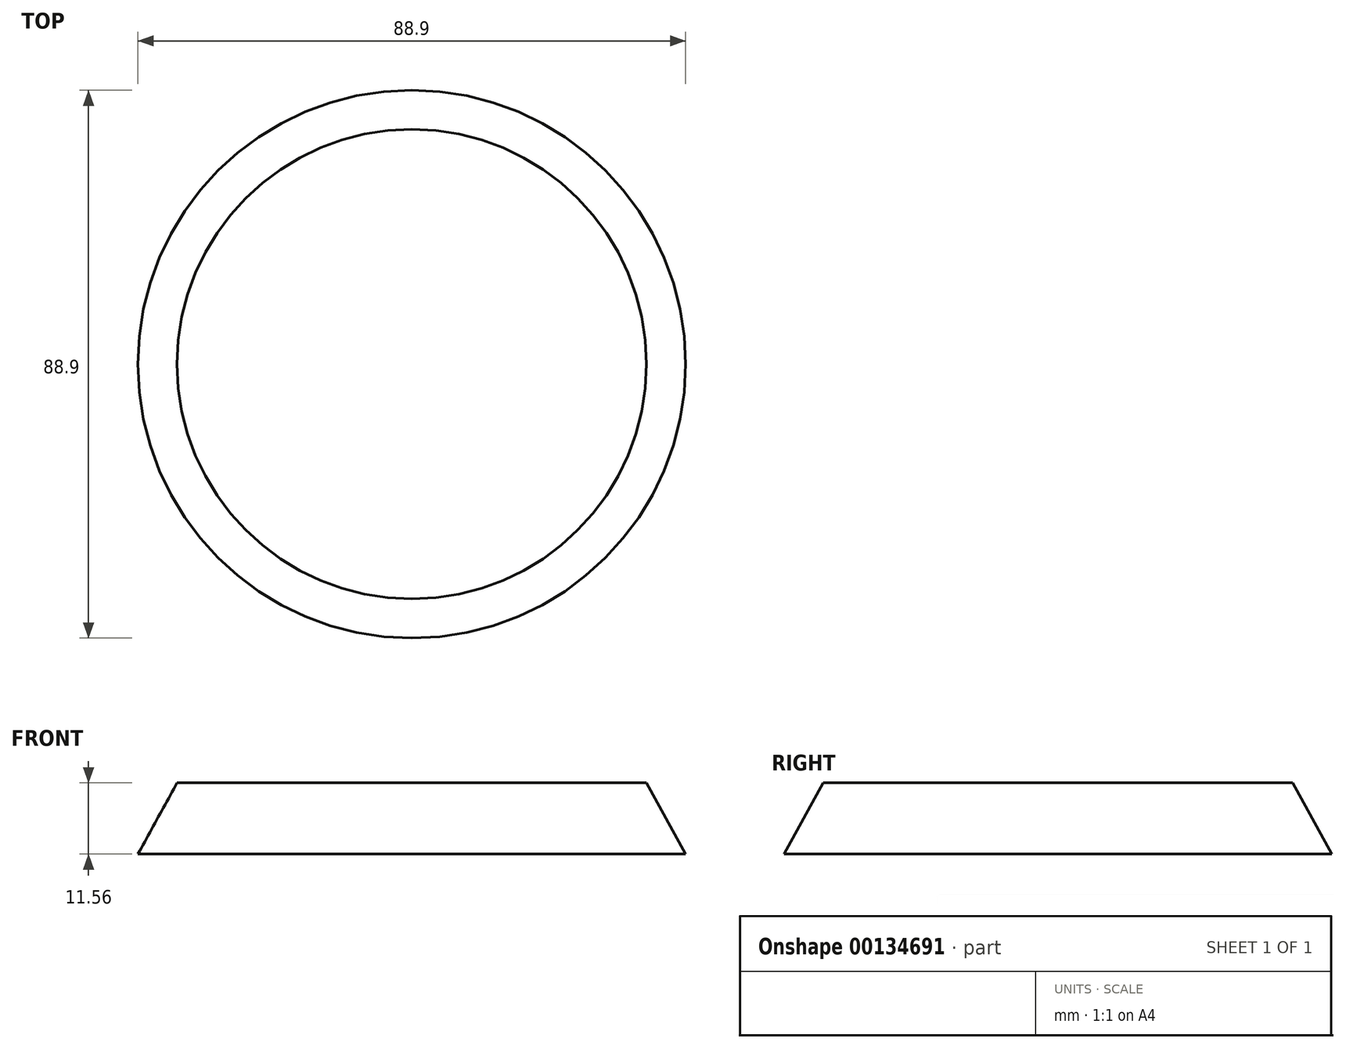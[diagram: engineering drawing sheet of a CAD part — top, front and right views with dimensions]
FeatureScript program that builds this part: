
annotation { "Feature Type Name" : "Feature", "Feature Type Description" : "" }
export const myFeature = defineFeature(function(context is Context, id is Id, definition is map)
    precondition{}
    {
        {
            var Q0;
            Q0=qCreatedBy(makeId("Front.planeOp"),FACE);
            var sketch = newSketch(context, id + "F0", { "sketchPlane" : qUnion([Q0])});
            skLineSegment(sketch, "E0", {"start": v(0, 11.56) * mm, "end": v(38.1, 11.56) * mm});
            skLineSegment(sketch, "E1", {"start": v(38.1, 11.56) * mm, "end": v(44.45, 0) * mm});
            skLineSegment(sketch, "E2", {"start": v(44.45, 0) * mm, "end": v(0, 0) * mm});
            skLineSegment(sketch, "E3", {"start": v(0, 0) * mm, "end": v(0, 11.56) * mm});
            skSolve(sketch);
        }
        {
            var Q0;
            Q0=makeQuery(id+"F0.imprint","IMPRINT",FACE,{"disambiguationData":[TD([[makeQuery(id+"F0.imprint","IMPRINT",EDGE,{"derivedFrom":sQuery(id+"F0.wireOp",EDGE,"E0")}),-1.0]])]});
            var Q1;
            Q1=sQuery(id+"F0.wireOp",EDGE,"E3");
            revolve(context, id + "F1", {"entities" : qUnion([Q0]), "axis" : qUnion([Q1]), "revolveType" : RevolveType.FULL});
        }
    });
